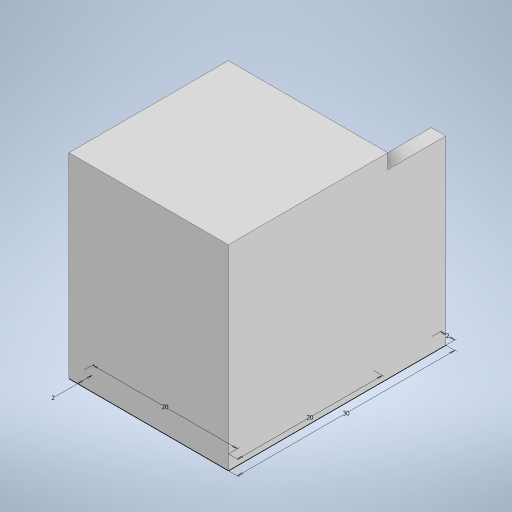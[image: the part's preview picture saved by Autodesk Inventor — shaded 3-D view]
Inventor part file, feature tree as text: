
AUTODESK INVENTOR PART (.ipt)
format: ipt  version: 2023.1 (Build 271208000, 208)  size: 201,216 bytes
history: native  units: mm
features: extrude x3, sketch x2
ambient origin geometry x8: Origin, YZ Plane, XZ Plane, XY Plane, X Axis, Y Axis, Z Axis, Center Point
bodies: Volumenkörper1 (feature_tree)
feature tree (5):
  sketch  "Skizze1"  dims[d0=2.0mm d1=30.0mm]
  extrude  "Extrusion1"  Depth=30.0mm
  extrude  "Extrusion2"  Depth=2.0mm
  extrude  "Extrusion3"  Depth=20.0mm
  sketch  "Skizze2"  dims[d2=20.0mm d3=2.0mm d4=20.0mm d5=2.0mm d6=0.0mm d7=25.0mm d8=0.0mm d9=2.0mm d10=0.0mm]
